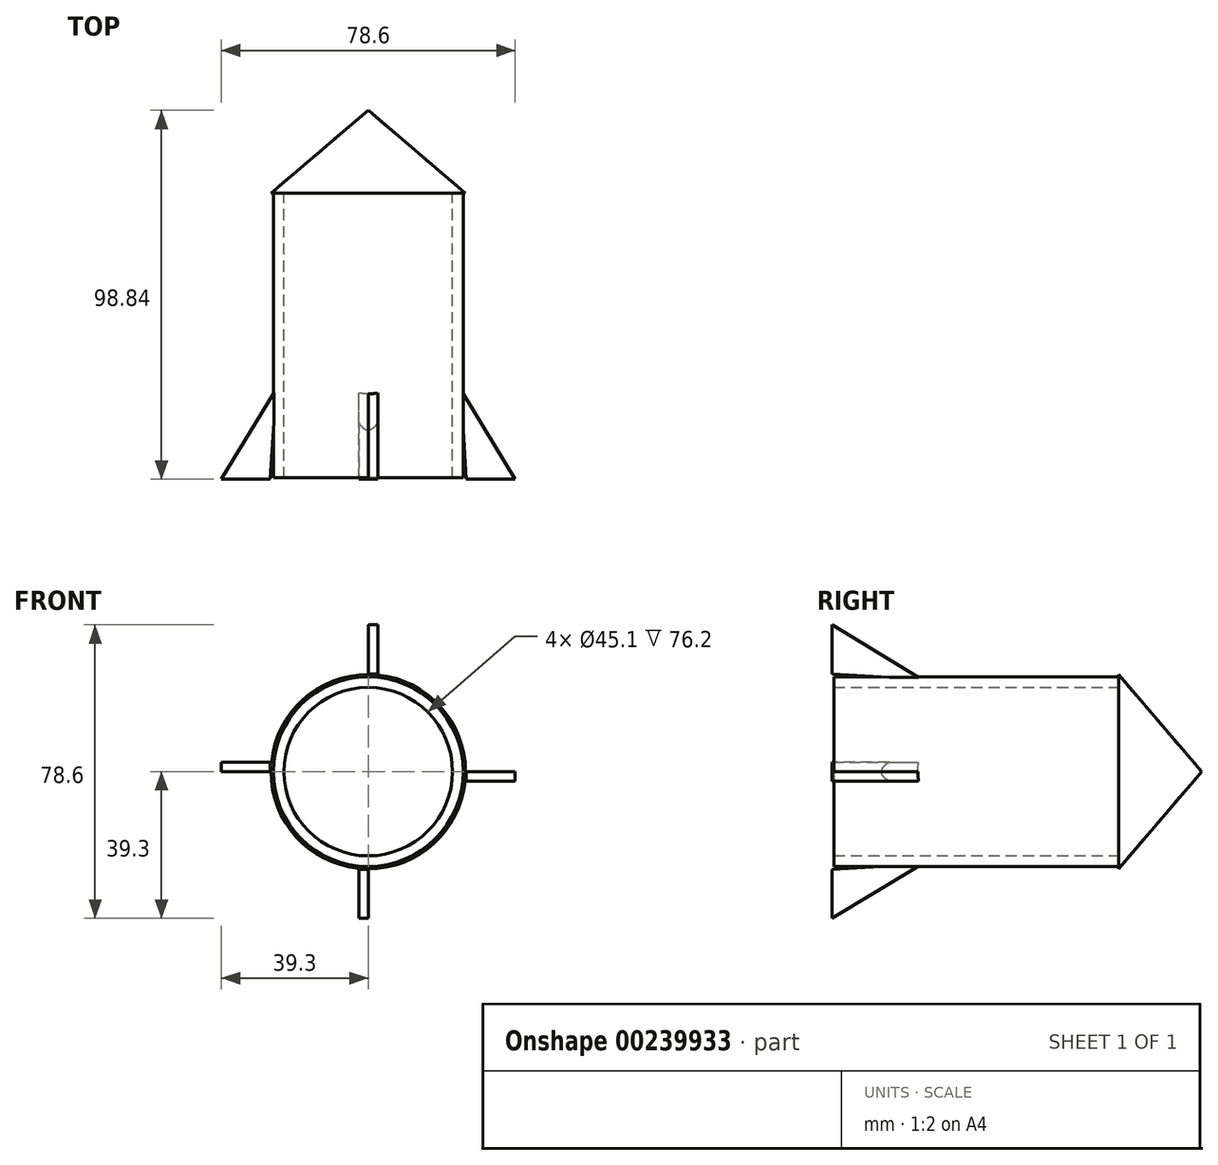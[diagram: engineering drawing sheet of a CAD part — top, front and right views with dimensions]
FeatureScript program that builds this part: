
annotation { "Feature Type Name" : "Feature", "Feature Type Description" : "" }
export const myFeature = defineFeature(function(context is Context, id is Id, definition is map)
    precondition{}
    {
        {
            var Q0;
            Q0=qCreatedBy(makeId("Front.planeOp"),FACE);
            var sketch = newSketch(context, id + "F0", { "sketchPlane" : qUnion([Q0])});
            skCircle(sketch, "E0", {"center": v(0, 0) * mm, "radius": 25.4 * mm});
            skSolve(sketch);
        }
        {
            var Q0;
            Q0 = qSketchRegion(id + "F0", true);
            extrude(context, id + "F1", {"entities" : qUnion([Q0]), "depth" : 76.2 * mm});
        }
        {
            var Q0;
            Q0=qCreatedBy(makeId("Front.planeOp"),FACE);
            var sketch = newSketch(context, id + "F2", { "sketchPlane" : qUnion([Q0])});
            skCircle(sketch, "E1", {"center": v(0, 0) * mm, "radius": 22.55 * mm});
            skSolve(sketch);
        }
        {
            var Q0;
            Q0 = qSketchRegion(id + "F2", true);
            extrude(context, id + "F3", {"entities" : qUnion([Q0]), "operationType" : NewBodyOperationType.REMOVE, "depth" : 76.2 * mm});
        }
        {
            var Q0;
            Q0=qCreatedBy(makeId("Top.planeOp"),FACE);
            var sketch = newSketch(context, id + "F4", { "sketchPlane" : qUnion([Q0])});
            skLineSegment(sketch, "E2", {"start": v(-26.18, -76.59) * mm, "end": v(-39.3, -76.59) * mm});
            skLineSegment(sketch, "E3", {"start": v(-39.3, -76.59) * mm, "end": v(-24.76, -52.63) * mm});
            skLineSegment(sketch, "E4", {"start": v(-24.76, -52.63) * mm, "end": v(-26.18, -76.59) * mm});
            skLineSegment(sketch, "E5", {"start": v(0, -76.59) * mm, "end": v(0, 0) * mm});
            skSolve(sketch);
        }
        {
            var Q0;
            Q0=makeQuery(id+"F4.imprint","IMPRINT",FACE,{"disambiguationData":[TD([[makeQuery(id+"F4.imprint","IMPRINT",EDGE,{"derivedFrom":sQuery(id+"F4.wireOp",EDGE,"E2")}),-1.0]])]});
            extrude(context, id + "F5", {"entities" : qUnion([Q0]), "operationType" : NewBodyOperationType.ADD, "depth" : 2.54 * mm});
        }
        {
            var Q0;
            Q0=qCreatedBy(makeId("Top.planeOp"),FACE);
            var sketch = newSketch(context, id + "F6", { "sketchPlane" : qUnion([Q0])});
            skLineSegment(sketch, "E6", {"start": v(-26.02, 0) * mm, "end": v(0, 22.25) * mm});
            skLineSegment(sketch, "E7", {"start": v(0, 22.25) * mm, "end": v(0, 0) * mm});
            skLineSegment(sketch, "E8", {"start": v(0, 0) * mm, "end": v(-26.02, 0) * mm});
            skSolve(sketch);
        }
        {
            var Q0;
            Q0 = qSketchRegion(id + "F6", true);
            var Q1;
            Q1=sQuery(id+"F6.wireOp",EDGE,"E7");
            revolve(context, id + "F7", {"operationType" : NewBodyOperationType.ADD, "entities" : qUnion([Q0]), "axis" : qUnion([Q1]), "revolveType" : RevolveType.FULL});
        }
        {
            var Q0;
            Q0=makeQuery(id+"F1.opExtrude","SWEPT_BODY",BODY,{"disambiguationData":[OSD([sQuery(id+"F0.wireOp",EDGE,"E0")])]});
            var Q1;
            Q1=makeQuery(id+"F3.boolean.opBoolean","COPY",FACE,{"derivedFrom":makeQuery(id+"F3.opExtrude","SWEPT_FACE",FACE,{"disambiguationData":[OSD([sQuery(id+"F2.wireOp",EDGE,"E1")])]})});
            circularPattern(context, id + "F8", {"entities" : qUnion([Q0]), "axis" : qUnion([Q1]), "angle" : 360 * degree, "instanceCount" : 4, "equalSpace" : true});
        }
    });
